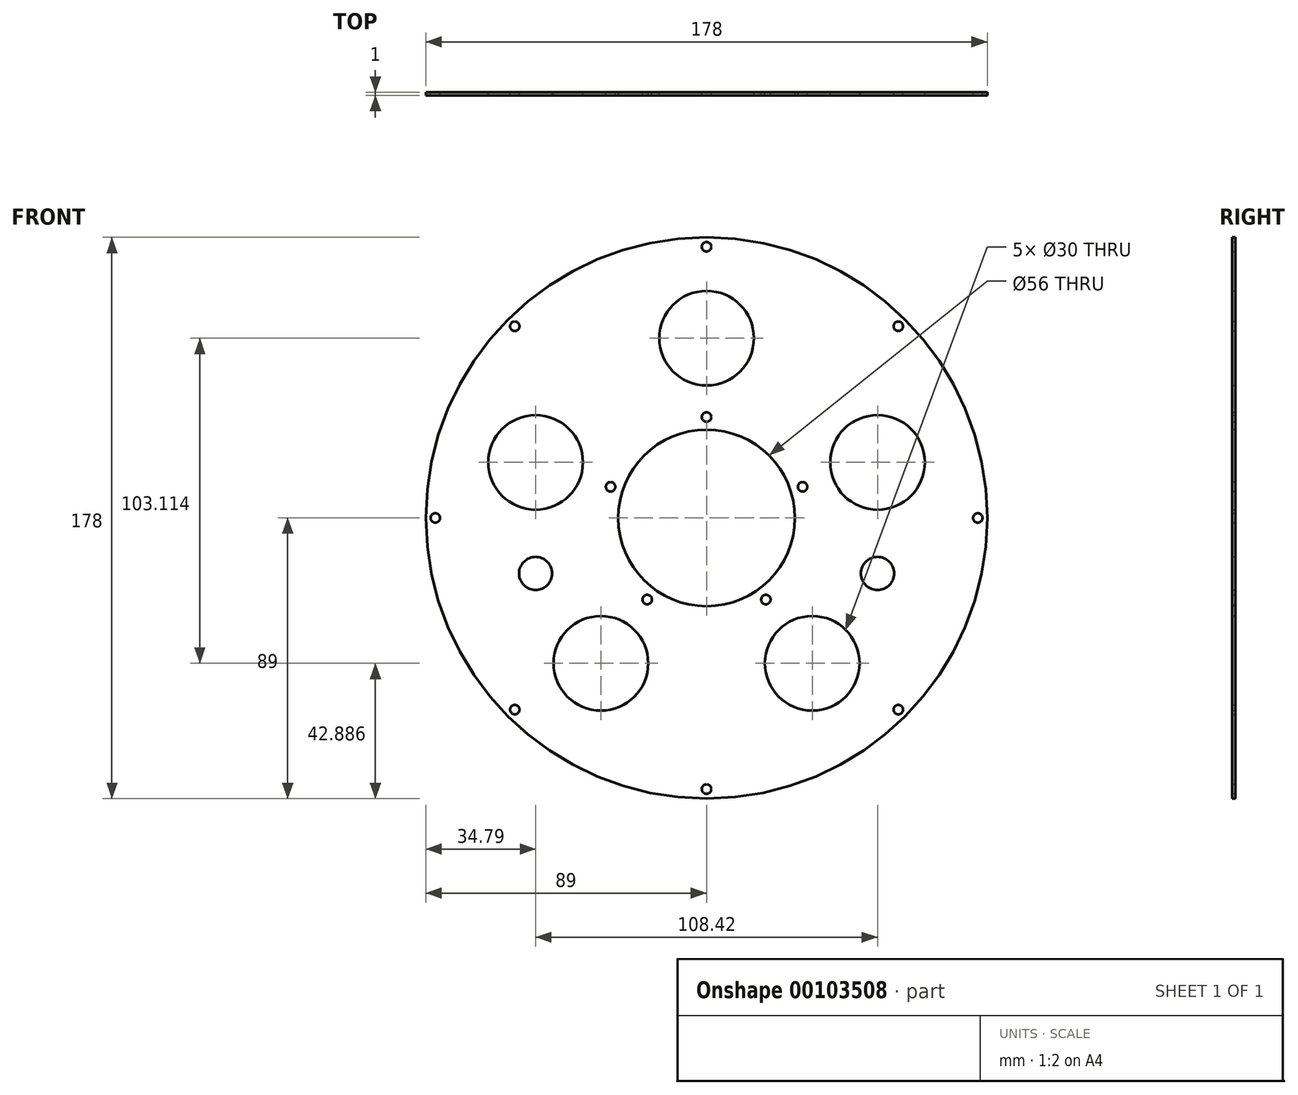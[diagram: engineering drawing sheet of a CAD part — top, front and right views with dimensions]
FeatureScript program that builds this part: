
annotation { "Feature Type Name" : "Feature", "Feature Type Description" : "" }
export const myFeature = defineFeature(function(context is Context, id is Id, definition is map)
    precondition{}
    {
        {
            var Q0;
            Q0=qCreatedBy(makeId("Front.planeOp"),FACE);
            var sketch = newSketch(context, id + "F0", { "sketchPlane" : qUnion([Q0])});
            skCircle(sketch, "E0", {"center": v(0, 0) * mm, "radius": 89 * mm});
            skCircle(sketch, "E1", {"center": v(0, 0) * mm, "radius": 28 * mm});
            skCircle(sketch, "E2", {"center": v(0, 0) * mm, "radius": 57 * mm, "construction": true});
            skLineSegment(sketch, "E3", {"start": v(0, 0) * mm, "end": v(0, 57) * mm, "construction": true});
            skLineSegment(sketch, "E4", {"start": v(0, 0) * mm, "end": v(-54.21, 17.61) * mm, "construction": true});
            skLineSegment(sketch, "E5", {"start": v(0, 0) * mm, "end": v(-54.21, -17.61) * mm, "construction": true});
            skPoint(sketch, "E6", {"position": v(0, 57) * mm});
            skPoint(sketch, "E7", {"position": v(-54.21, 17.61) * mm});
            skPoint(sketch, "E8", {"position": v(-54.21, -17.61) * mm});
            skPoint(sketch, "E9", {"position": v(54.21, -17.61) * mm});
            skPoint(sketch, "E10", {"position": v(54.21, 17.61) * mm});
            skPoint(sketch, "E11", {"position": v(-33.5, -46.11) * mm});
            skPoint(sketch, "E12", {"position": v(33.5, -46.11) * mm});
            skCircle(sketch, "E13", {"center": v(0, 0) * mm, "radius": 32 * mm, "construction": true});
            skLineSegment(sketch, "E14", {"start": v(0, 0) * mm, "end": v(0, -32) * mm, "construction": true});
            skLineSegment(sketch, "E15", {"start": v(54.21, 17.61) * mm, "end": v(0, 0) * mm, "construction": true});
            skLineSegment(sketch, "E16", {"start": v(0, 0) * mm, "end": v(33.5, -46.11) * mm, "construction": true});
            skLineSegment(sketch, "E17", {"start": v(0, 0) * mm, "end": v(-33.5, -46.11) * mm, "construction": true});
            skPoint(sketch, "E18", {"position": v(-30.43, 9.89) * mm});
            skPoint(sketch, "E19", {"position": v(0, 32) * mm});
            skPoint(sketch, "E20", {"position": v(30.43, 9.89) * mm});
            skPoint(sketch, "E21", {"position": v(18.8, -25.89) * mm});
            skPoint(sketch, "E22", {"position": v(-18.8, -25.89) * mm});
            skSolve(sketch);
        }
        {
            var Q0;
            Q0=makeQuery(id+"F0.imprint","IMPRINT",FACE,{"disambiguationData":[TD([[makeQuery(id+"F0.imprint","IMPRINT",EDGE,{"derivedFrom":sQuery(id+"F0.wireOp",EDGE,"E0")}),1.0]])]});
            extrude(context, id + "F1", {"entities" : qUnion([Q0]), "oppositeDirection" : true, "depth" : 1 * mm});
        }
        {
            var Q0;
            Q0=sQuery(id+"F0.wireOp",VERTEX,"E8");
            var Q1;
            Q1=sQuery(id+"F0.wireOp",VERTEX,"E9");
            var Q2;
            Q2=makeQuery(id+"F1.opExtrude","SWEPT_BODY",BODY,{"disambiguationData":[OSD([sQuery(id+"F0.wireOp",EDGE,"E0"),sQuery(id+"F0.wireOp",EDGE,"E1")])]});
            hole(context, id + "F2", {"style" : HoleStyle.SIMPLE, "endStyle" : HoleEndStyle.THROUGH, "standardTappedOrClearance" : lookupTablePath({ "standard" : "ISO", "size" : "10.5", "type" : "Drilled" }), "standardBlindInLast" : lookupTablePath({ "standard" : "ISO", "size" : "10.5", "type" : "Drilled" }), "holeDiameter" : 10.5 * mm, "locations" : qUnion([Q0, Q1]), "scope" : qUnion([Q2]), "isTappedThrough" : true, "startStyle" : HoleStartStyle.SKETCH});
        }
        {
            var Q0;
            Q0=sQuery(id+"F0.wireOp",VERTEX,"E7");
            var Q1;
            Q1=sQuery(id+"F0.wireOp",VERTEX,"E6");
            var Q2;
            Q2=sQuery(id+"F0.wireOp",VERTEX,"E10");
            var Q3;
            Q3=sQuery(id+"F0.wireOp",VERTEX,"E12");
            var Q4;
            Q4=sQuery(id+"F0.wireOp",VERTEX,"E11");
            var Q5;
            Q5=makeQuery(id+"F1.opExtrude","SWEPT_BODY",BODY,{"disambiguationData":[OSD([sQuery(id+"F0.wireOp",EDGE,"E0"),sQuery(id+"F0.wireOp",EDGE,"E1")])]});
            hole(context, id + "F3", {"style" : HoleStyle.SIMPLE, "endStyle" : HoleEndStyle.THROUGH, "standardTappedOrClearance" : lookupTablePath({ "standard" : "ISO", "size" : "30", "type" : "Drilled" }), "standardBlindInLast" : lookupTablePath({ "standard" : "ISO", "size" : "30", "type" : "Drilled" }), "holeDiameter" : 30 * mm, "locations" : qUnion([Q0, Q1, Q2, Q3, Q4]), "scope" : qUnion([Q5]), "isTappedThrough" : true, "startStyle" : HoleStartStyle.SKETCH});
        }
        {
            var Q0;
            Q0=sQuery(id+"F0.wireOp",VERTEX,"E18");
            var Q1;
            Q1=sQuery(id+"F0.wireOp",VERTEX,"E19");
            var Q2;
            Q2=sQuery(id+"F0.wireOp",VERTEX,"E20");
            var Q3;
            Q3=sQuery(id+"F0.wireOp",VERTEX,"E21");
            var Q4;
            Q4=sQuery(id+"F0.wireOp",VERTEX,"E22");
            var Q5;
            Q5=makeQuery(id+"F1.opExtrude","SWEPT_BODY",BODY,{"disambiguationData":[OSD([sQuery(id+"F0.wireOp",EDGE,"E0"),sQuery(id+"F0.wireOp",EDGE,"E1")])]});
            hole(context, id + "F4", {"style" : HoleStyle.SIMPLE, "endStyle" : HoleEndStyle.THROUGH, "standardTappedOrClearance" : lookupTablePath({ "standard" : "ISO", "size" : "3", "type" : "Drilled" }), "standardBlindInLast" : lookupTablePath({ "standard" : "ISO", "size" : "3", "type" : "Drilled" }), "holeDiameter" : 3 * mm, "locations" : qUnion([Q0, Q1, Q2, Q3, Q4]), "scope" : qUnion([Q5]), "isTappedThrough" : true, "startStyle" : HoleStartStyle.SKETCH});
        }
        {
            var Q0;
            Q0=makeQuery(id+"F1.opExtrude","CAP_FACE",FACE,{"disambiguationData":[OSD([sQuery(id+"F0.wireOp",EDGE,"E0"),sQuery(id+"F0.wireOp",EDGE,"E1")])],"isStart":true});
            var sketch = newSketch(context, id + "F5", { "sketchPlane" : qUnion([Q0])});
            skCircle(sketch, "E23", {"center": v(0, 0) * mm, "radius": 86 * mm});
            skLineSegment(sketch, "E24", {"start": v(0, 86) * mm, "end": v(0, -86) * mm, "construction": true});
            skLineSegment(sketch, "E25", {"start": v(86, 0) * mm, "end": v(-86, 0) * mm, "construction": true});
            skLineSegment(sketch, "E26", {"start": v(60.81, 60.81) * mm, "end": v(-60.81, -60.81) * mm, "construction": true});
            skLineSegment(sketch, "E27", {"start": v(-60.81, 60.81) * mm, "end": v(60.81, -60.81) * mm, "construction": true});
            skSolve(sketch);
        }
        {
            var Q0;
            Q0=sQuery(id+"F5.wireOp",VERTEX,"E27.start");
            var Q1;
            Q1=sQuery(id+"F5.wireOp",VERTEX,"E24.start");
            var Q2;
            Q2=sQuery(id+"F5.wireOp",VERTEX,"E26.start");
            var Q3;
            Q3=sQuery(id+"F5.wireOp",VERTEX,"E25.start");
            var Q4;
            Q4=sQuery(id+"F5.wireOp",VERTEX,"E27.end");
            var Q5;
            Q5=sQuery(id+"F5.wireOp",VERTEX,"E24.end");
            var Q6;
            Q6=sQuery(id+"F5.wireOp",VERTEX,"E26.end");
            var Q7;
            Q7=sQuery(id+"F5.wireOp",VERTEX,"E25.end");
            var Q8;
            Q8=makeQuery(id+"F1.opExtrude","SWEPT_BODY",BODY,{"disambiguationData":[OSD([sQuery(id+"F0.wireOp",EDGE,"E0"),sQuery(id+"F0.wireOp",EDGE,"E1")])]});
            hole(context, id + "F6", {"style" : HoleStyle.SIMPLE, "endStyle" : HoleEndStyle.THROUGH, "standardTappedOrClearance" : lookupTablePath({ "standard" : "ISO", "size" : "3", "type" : "Drilled" }), "standardBlindInLast" : lookupTablePath({ "standard" : "ISO", "size" : "3", "type" : "Drilled" }), "holeDiameter" : 3 * mm, "locations" : qUnion([Q0, Q1, Q2, Q3, Q4, Q5, Q6, Q7]), "scope" : qUnion([Q8]), "isTappedThrough" : true, "startStyle" : HoleStartStyle.SKETCH});
        }
    });
